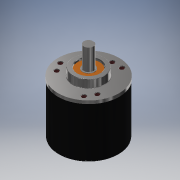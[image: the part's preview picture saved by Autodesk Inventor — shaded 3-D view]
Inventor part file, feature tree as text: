
AUTODESK INVENTOR PART (.ipt)
format: ipt  version: 2019 (Build 230136000, 136)  size: 242,688 bytes
history: native  units: mm
features: extrude x10, sketch x10, thread x6, fillet x2, chamfer x2, plane x2
ambient origin geometry x8: Origin, YZ Plane, XZ Plane, XY Plane, X Axis, Y Axis, Z Axis, Center Point
bodies: Solid1 (feature_tree)
feature tree (32):
  extrude  "Extrusion1"  Depth=1.0mm
  fillet  "Fillet1"  Radius=2.0mm
  extrude  "Extrusion2"  Depth=5.0mm TaperAngle=0.0deg
  extrude  "Extrusion3"  Depth=13.4mm TaperAngle=0.0deg
  extrude  "Extrusion4"  Depth=10.0mm
  extrude  "Extrusion5"  Depth=3.8mm TaperAngle=0.0deg
  extrude  "Extrusion6"  Depth=30.0mm TaperAngle=360.0deg
  extrude  "Extrusion7"  Depth=10.0mm TaperAngle=0.0deg
  fillet  "Fillet2"  Radius=10.0mm
  chamfer  "Chamfer1"  Distance=10.0mm
  extrude  "Extrusion8"  Depth=10.0mm TaperAngle=0.0deg
  extrude  "Extrusion9"  Depth=5.0mm TaperAngle=45.0deg
  thread  "Thread1"  [1 undecoded]
  thread  "Thread2"  [1 undecoded]
  thread  "Thread3"  [1 undecoded]
  thread  "Thread4"  [1 undecoded]
  thread  "Thread5"  [1 undecoded]
  thread  "Thread6"  [1 undecoded]
  chamfer  "Chamfer2"  [1 undecoded]
  plane  "Work Plane2"
  extrude  "Extrusion10"  [1 undecoded]
  sketch  "Sketch1"  dims[d1=34.12mm d2=0.0mm d3=1.0mm d5=2.0mm d6=0.0mm]
  sketch  "Sketch2"  dims[d8=5.0mm d9=0.0mm d11=5.0mm d12=0.0mm]
  sketch  "Sketch3"  dims[d14=4.0mm d15=0.0mm d17=13.4mm d18=0.0mm]
  sketch  "Sketch4"  dims[d20=10.0mm d21=0.0mm d22=0.3mm]
  sketch  "Sketch5"  dims[d23=0.3mm d24=2.0mm d25=45.0deg d27=3.8mm d28=0.0mm]
  sketch  "Sketch6"  dims[d30=30.0mm d32=360.0deg d36=30.0mm d38=360.0deg]
  sketch  "Sketch7"  dims[d40=5.0mm d41=0.0mm d42=10.0mm d43=0.0mm d44=10.0mm d45=0.0mm d46=10.0mm d47=0.0mm]
  sketch  "Sketch8"  dims[d48=10.0mm d49=0.0mm d50=10.0mm d51=0.0mm]
  sketch  "Sketch9"  dims[d52=10.0mm d53=0.0mm d54=0.3mm d55=2.0mm d56=45.0deg d57=19.12mm d58=2.0mm d62=5.0mm d63=0.0mm]
  plane  "Work Plane1"
  sketch  "Sketch10"
note: 8 required parameter values undecoded (feature->parameter linkage not recoverable at this tier; creation-order binding heuristic only, values carry confidence <= 0.55)
